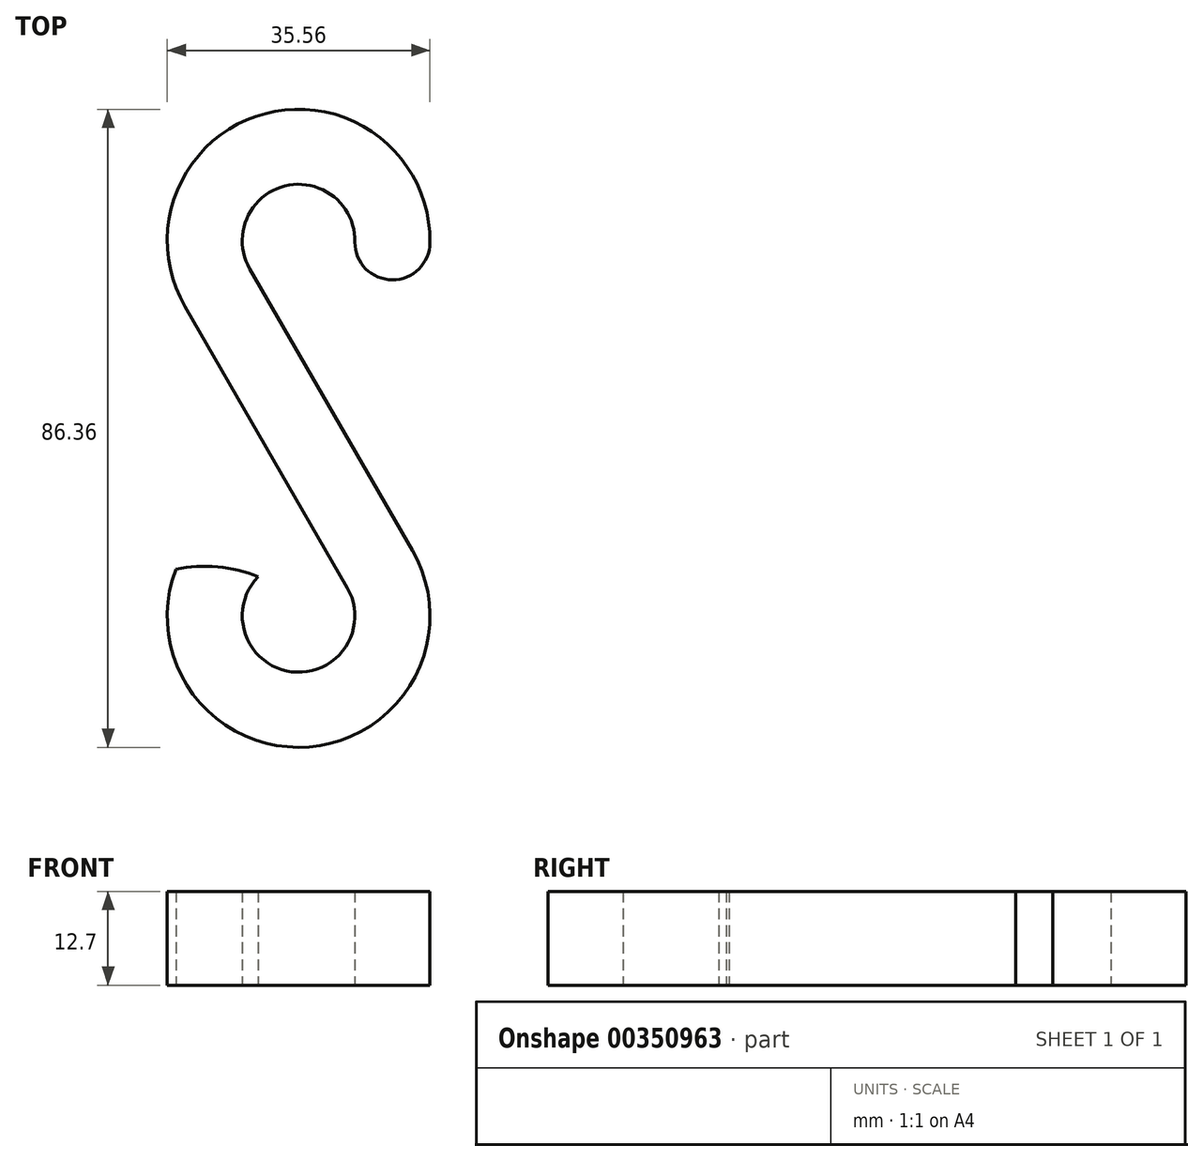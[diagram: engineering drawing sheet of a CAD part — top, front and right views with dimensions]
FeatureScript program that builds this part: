
annotation { "Feature Type Name" : "Feature", "Feature Type Description" : "" }
export const myFeature = defineFeature(function(context is Context, id is Id, definition is map)
    precondition{}
    {
        {
            var Q0;
            Q0=qCreatedBy(makeId("Top.planeOp"),FACE);
            var sketch = newSketch(context, id + "F0", { "sketchPlane" : qUnion([Q0])});
            skLineSegment(sketch, "E0", {"start": v(-15.4, 16.5) * mm, "end": v(6.6, -21.59) * mm});
            skLineSegment(sketch, "E1", {"start": v(-6.6, 21.59) * mm, "end": v(8.83, -5.14) * mm});
            skArc(sketch, "E2", {"start": v(7.62, 25.19) * mm, "mid": v(-1.87, 32.79) * mm, "end": v(-6.6, 21.6) * mm});
            skArc(sketch, "E3", {"start": v(17.78, 25.15) * mm, "mid": v(-4.48, 42.6) * mm, "end": v(-15.4, 16.51) * mm});
            skLineSegment(sketch, "E4", {"start": v(6.6, -21.59) * mm, "end": v(6.6, -21.59) * mm});
            skArc(sketch, "E5", {"start": v(-5.47, -20.1) * mm, "mid": v(-0.94, -32.96) * mm, "end": v(6.6, -21.6) * mm});
            skArc(sketch, "E6", {"start": v(-16.62, -19.07) * mm, "mid": v(1.42, -43.12) * mm, "end": v(15.4, -16.51) * mm});
            skArc(sketch, "E7", {"start": v(-5.47, -20.1) * mm, "mid": v(-10.97, -18.75) * mm, "end": v(-16.62, -19.07) * mm});
            skArc(sketch, "E8", {"start": v(7.62, 25.19) * mm, "mid": v(12.68, 20.09) * mm, "end": v(17.78, 25.15) * mm});
            skLineSegment(sketch, "E9", {"start": v(8.83, -5.14) * mm, "end": v(15.4, -16.5) * mm});
            skSolve(sketch);
        }
        {
            var Q0;
            Q0 = qSketchRegion(id + "F0", true);
            extrude(context, id + "F1", {"entities" : qUnion([Q0]), "depth" : 12.7 * mm});
        }
    });
